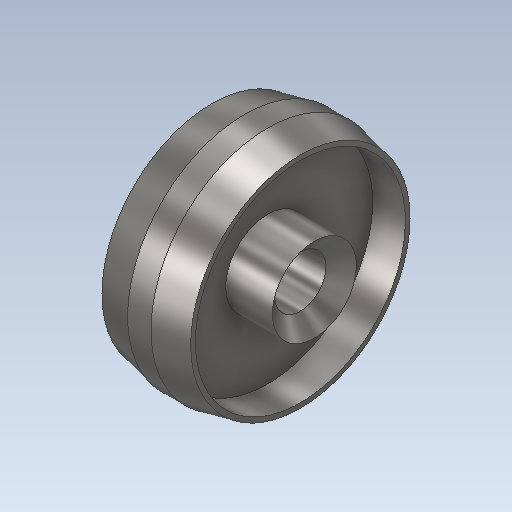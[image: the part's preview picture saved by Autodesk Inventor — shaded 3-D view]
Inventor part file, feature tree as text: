
AUTODESK INVENTOR PART (.ipt)
format: ipt  version: 2020 (Build 240168000, 168)  size: 194,048 bytes
history: native  units: mm
features: revolve x1, sketch x1
ambient origin geometry x8: Origin, YZ Plane, XZ Plane, XY Plane, X Axis, Y Axis, Z Axis, Center Point
bodies: Solid1 (feature_tree)
feature tree (2):
  revolve  "Revolution1"  [1 undecoded]
  sketch  "Sketch1"  dims[d0=50.0mm d1=18.0mm d2=38.0mm d3=11.0mm d4=39.0mm d5=27.0mm d8=10.0mm d9=20.0mm d10=90.0deg d11=34.0mm d12=2.0mm d13=2.0mm d14=18.0mm d15=26.248585mm d16=11.714245mm d17=18.0mm d18=45.0mm]
note: 1 required parameter value undecoded (feature->parameter linkage not recoverable at this tier; creation-order binding heuristic only, values carry confidence <= 0.55)
